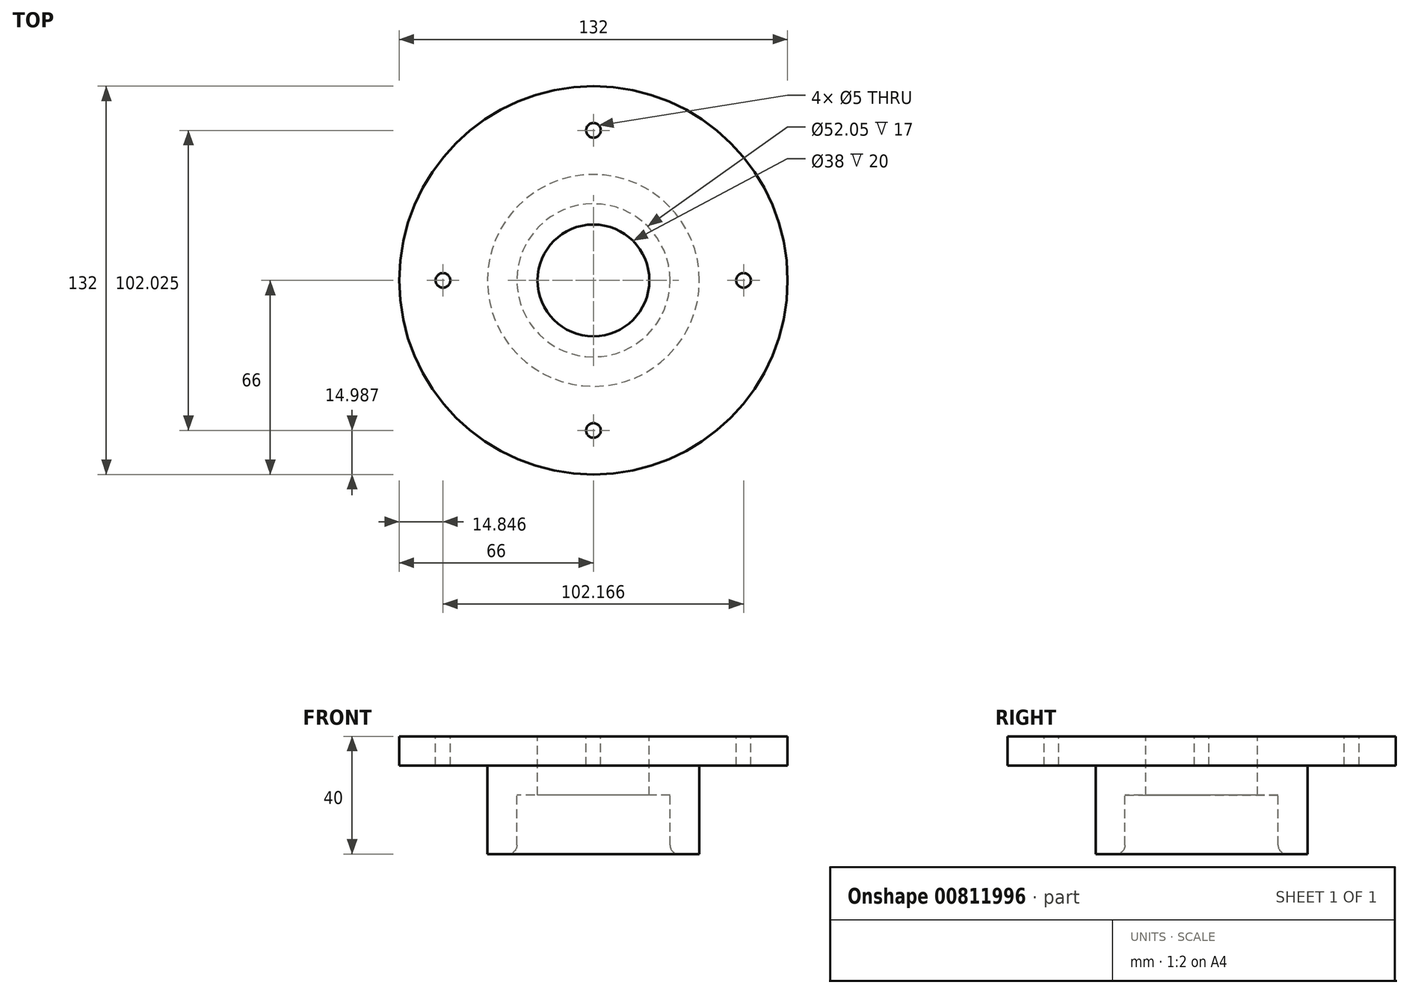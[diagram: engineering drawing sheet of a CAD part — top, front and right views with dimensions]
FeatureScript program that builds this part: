
annotation { "Feature Type Name" : "Feature", "Feature Type Description" : "" }
export const myFeature = defineFeature(function(context is Context, id is Id, definition is map)
    precondition{}
    {
        {
            var Q0;
            Q0=qCreatedBy(makeId("Front.planeOp"),FACE);
            var sketch = newSketch(context, id + "F0", { "sketchPlane" : qUnion([Q0])});
            skLineSegment(sketch, "E0", {"start": v(0, 34.1) * mm, "end": v(0, -48.5) * mm, "construction": true});
            skLineSegment(sketch, "E1", {"start": v(-26.02, 0) * mm, "end": v(-26.03, 20) * mm});
            skLineSegment(sketch, "E2", {"start": v(-26.02, 0) * mm, "end": v(-36.02, 0) * mm});
            skPoint(sketch, "E3.end.orphan", {"position": v(0, 20) * mm});
            skPoint(sketch, "E4.end.orphan", {"position": v(0, 36.52) * mm});
            skLineSegment(sketch, "E5", {"start": v(-26.03, 20) * mm, "end": v(-19, 20) * mm});
            skLineSegment(sketch, "E6", {"start": v(-19, 20) * mm, "end": v(-19, 40) * mm});
            skLineSegment(sketch, "E7", {"start": v(-19, 40) * mm, "end": v(-66, 40) * mm});
            skPoint(sketch, "E8", {"position": v(-51, 0) * mm});
            skPoint(sketch, "E9", {"position": v(-51, 40) * mm});
            skLineSegment(sketch, "E10", {"start": v(-66, 30) * mm, "end": v(-36.03, 30) * mm});
            skLineSegment(sketch, "E11", {"start": v(-36.03, 30) * mm, "end": v(-36.02, 0) * mm});
            skPoint(sketch, "E12.end.orphan", {"position": v(-76, 40) * mm});
            skPoint(sketch, "E12.start.orphan", {"position": v(-75.97, 0) * mm});
            skLineSegment(sketch, "E13", {"start": v(-66, 30) * mm, "end": v(-66, 40) * mm});
            skSolve(sketch);
        }
        {
            var Q0;
            Q0 = qSketchRegion(id + "F0", true);
            var Q1;
            Q1=sQuery(id+"F0.wireOp",EDGE,"E0");
            revolve(context, id + "F1", {"surfaceOperationType" : NewSurfaceOperationType.NEW, "entities" : qUnion([Q0]), "axis" : qUnion([Q1]), "revolveType" : RevolveType.FULL});
        }
        {
            var Q0;
            Q0=makeQuery(id+"F1.opRevolve","SWEPT_FACE",FACE,{"disambiguationData":[OSD([sQuery(id+"F0.wireOp",EDGE,"E7")])]});
            cPlane(context, id + "F2", {"entities" : qUnion([Q0]), "cplaneType" : CPlaneType.OFFSET, "offset" : 0 * mm, "width" : 150 * mm, "height" : 150 * mm});
        }
        {
            var Q0;
            Q0=qCreatedBy(id+"F2.planeOp",FACE);
            var sketch = newSketch(context, id + "F3", { "sketchPlane" : qUnion([Q0])});
            skCircle(sketch, "E14.0", {"center": v(0, 0) * mm, "radius": 66 * mm});
            skCircle(sketch, "E14.1", {"center": v(0, 0) * mm, "radius": 36.02 * mm});
            skLineSegment(sketch, "E15", {"start": v(36.02, 0) * mm, "end": v(66, 0) * mm, "construction": true});
            skLineSegment(sketch, "E16", {"start": v(-36.02, 0) * mm, "end": v(-66, 0) * mm, "construction": true});
            skPoint(sketch, "E17", {"position": v(51.01, 0) * mm});
            skPoint(sketch, "E18", {"position": v(-51.01, 0) * mm});
            skSolve(sketch);
        }
        {
            var Q0;
            Q0=makeQuery(id+"F3.imprint","IMPRINT",FACE,{"disambiguationData":[TD([[makeQuery(id+"F3.imprint","IMPRINT",EDGE,{"derivedFrom":sQuery(id+"F3.wireOp",EDGE,"E14.0")}),1.0]])]});
            var sketch = newSketch(context, id + "F4", { "sketchPlane" : qUnion([Q0])});
            skCircle(sketch, "E19.0", {"center": v(0, 0) * mm, "radius": 66 * mm});
            skCircle(sketch, "E20.0", {"center": v(0, 0) * mm, "radius": 19 * mm});
            skCircle(sketch, "E21.0", {"center": v(0, 0) * mm, "radius": 36.02 * mm});
            skLineSegment(sketch, "E22", {"start": v(0, -66) * mm, "end": v(0, -36.02) * mm, "construction": true});
            skLineSegment(sketch, "E23", {"start": v(0, -36.02) * mm, "end": v(0, 36.02) * mm, "construction": true});
            skLineSegment(sketch, "E24", {"start": v(0, 36.02) * mm, "end": v(0, 66) * mm, "construction": true});
            skPoint(sketch, "E25", {"position": v(0, -51.01) * mm});
            skPoint(sketch, "E26", {"position": v(0, 51.01) * mm});
            skSolve(sketch);
        }
        {
            var Q0;
            Q0=sQuery(id+"F4.wireOp",VERTEX,"E26");
            var Q1;
            Q1=sQuery(id+"F4.wireOp",VERTEX,"E25");
            var Q2;
            Q2=makeQuery(id+"F1.opRevolve","SWEPT_BODY",BODY,{"disambiguationData":[OSD([sQuery(id+"F0.wireOp",EDGE,"E1"),sQuery(id+"F0.wireOp",EDGE,"E2"),sQuery(id+"F0.wireOp",EDGE,"E12"),sQuery(id+"F0.wireOp",EDGE,"E5"),sQuery(id+"F0.wireOp",EDGE,"E6"),sQuery(id+"F0.wireOp",EDGE,"E7"),sQuery(id+"F0.wireOp",EDGE,"HfGTnwyy-LNjW-t2LW-5Ada-AqDmC1wUwWpH"),sQuery(id+"F0.wireOp",EDGE,"E10"),sQuery(id+"F0.wireOp",EDGE,"E11"),sQuery(id+"F0.wireOp",EDGE,"76d73de7-15df-4280-85dd-0e16687f294b.trimOffspring")])]});
            hole(context, id + "F5", {"style" : HoleStyle.SIMPLE, "endStyle" : HoleEndStyle.THROUGH, "holeDiameter" : 5 * mm, "majorDiameter" : 5 * mm, "isTappedThrough" : true, "tappedDepth" : 12 * mm, "tapClearance" : 3, "locations" : qUnion([Q0, Q1]), "scope" : qUnion([Q2])});
        }
        {
            var Q0;
            Q0=makeQuery(id+"F1.opRevolve","SWEPT_EDGE",EDGE,{"disambiguationData":[OSD([sQuery(id+"F0.wireOp",EDGE,"E1"),sQuery(id+"F0.wireOp",EDGE,"E2")])]});
            fillet(context, id + "F6", {"entities" : qUnion([Q0]), "radius" : 3 * mm, "tangentPropagation" : true, "allowEdgeOverflow" : false});
        }
        {
            var Q0;
            Q0=makeQuery(id+"F3.imprint","IMPRINT",FACE,{"disambiguationData":[TD([[makeQuery(id+"F3.imprint","IMPRINT",EDGE,{"derivedFrom":sQuery(id+"F3.wireOp",EDGE,"E14.0")}),1.0]])]});
            var sketch = newSketch(context, id + "F7", { "sketchPlane" : qUnion([Q0])});
            skPoint(sketch, "E27", {"position": v(51.15, 0) * mm});
            skPoint(sketch, "E28", {"position": v(-51.15, 0) * mm});
            skSolve(sketch);
        }
        {
            var Q0;
            Q0=sQuery(id+"F3.wireOp",VERTEX,"E17");
            var Q1;
            Q1=sQuery(id+"F7.wireOp",VERTEX,"E28");
            var Q2;
            Q2=makeQuery(id+"F1.opRevolve","SWEPT_BODY",BODY,{"disambiguationData":[OSD([sQuery(id+"F0.wireOp",EDGE,"E1"),sQuery(id+"F0.wireOp",EDGE,"E2"),sQuery(id+"F0.wireOp",EDGE,"E5"),sQuery(id+"F0.wireOp",EDGE,"E6"),sQuery(id+"F0.wireOp",EDGE,"E7"),sQuery(id+"F0.wireOp",EDGE,"E10"),sQuery(id+"F0.wireOp",EDGE,"E11"),sQuery(id+"F0.wireOp",EDGE,"E13")])]});
            hole(context, id + "F8", {"style" : HoleStyle.SIMPLE, "endStyle" : HoleEndStyle.THROUGH, "holeDiameter" : 5 * mm, "majorDiameter" : 5 * mm, "isTappedThrough" : true, "tappedDepth" : 12 * mm, "tapClearance" : 3, "locations" : qUnion([Q0, Q1]), "scope" : qUnion([Q2])});
        }
    });
